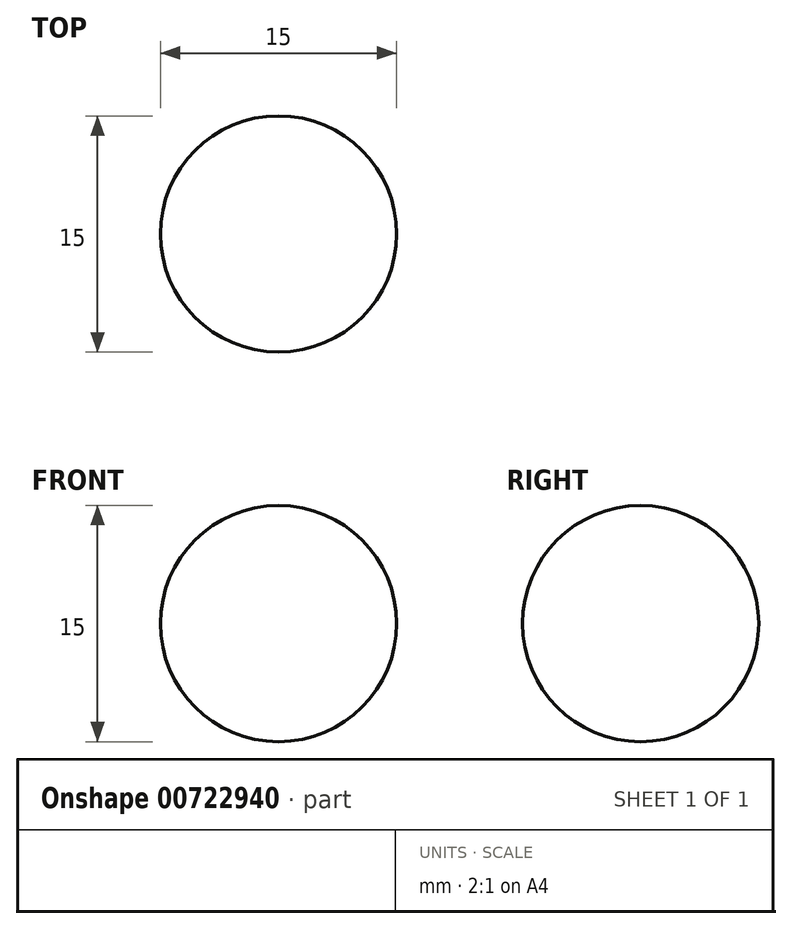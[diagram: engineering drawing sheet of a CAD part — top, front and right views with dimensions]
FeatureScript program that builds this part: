
annotation { "Feature Type Name" : "Feature", "Feature Type Description" : "" }
export const myFeature = defineFeature(function(context is Context, id is Id, definition is map)
    precondition{}
    {
        {
            var Q0;
            Q0=qCreatedBy(makeId("Front.planeOp"),FACE);
            var sketch = newSketch(context, id + "F0", { "sketchPlane" : qUnion([Q0])});
            skCircle(sketch, "E0", {"center": v(0, 0) * mm, "radius": 7.5 * mm});
            skSolve(sketch);
        }
        {
            var Q0;
            Q0=makeQuery(id+"F0.imprint","IMPRINT",FACE,{"disambiguationData":[TD([[makeQuery(id+"F0.imprint","IMPRINT",EDGE,{"derivedFrom":sQuery(id+"F0.wireOp",EDGE,"E0")}),1.0]])]});
            extrude(context, id + "F1", {"entities" : qUnion([Q0]), "depth" : 7.5 * mm, "offsetDistance" : 25 * mm});
        }
        {
            var Q0;
            Q0=makeQuery(id+"F1.opExtrude","CAP_FACE",FACE,{"disambiguationData":[OSD([sQuery(id+"F0.wireOp",EDGE,"E0")])],"isStart":false});
            fillet(context, id + "F2", {"entities" : qUnion([Q0]), "radius" : 7.5 * mm, "tangentPropagation" : true, "allowEdgeOverflow" : false});
        }
        {
            var Q0;
            Q0=makeQuery(id+"F1.opExtrude","CAP_FACE",FACE,{"disambiguationData":[OSD([sQuery(id+"F0.wireOp",EDGE,"E0")])],"isStart":true});
            extrude(context, id + "F3", {"entities" : qUnion([Q0]), "operationType" : NewBodyOperationType.ADD, "depth" : 7.5 * mm, "offsetDistance" : 25 * mm});
        }
        {
            var Q0;
            Q0=makeQuery(id+"F3.opExtrude","CAP_FACE",FACE,{"disambiguationData":[OSD([sQuery(id+"F0.wireOp",EDGE,"E0")])],"isStart":false});
            fillet(context, id + "F4", {"entities" : qUnion([Q0]), "radius" : 7.5 * mm, "tangentPropagation" : true, "allowEdgeOverflow" : false});
        }
    });
